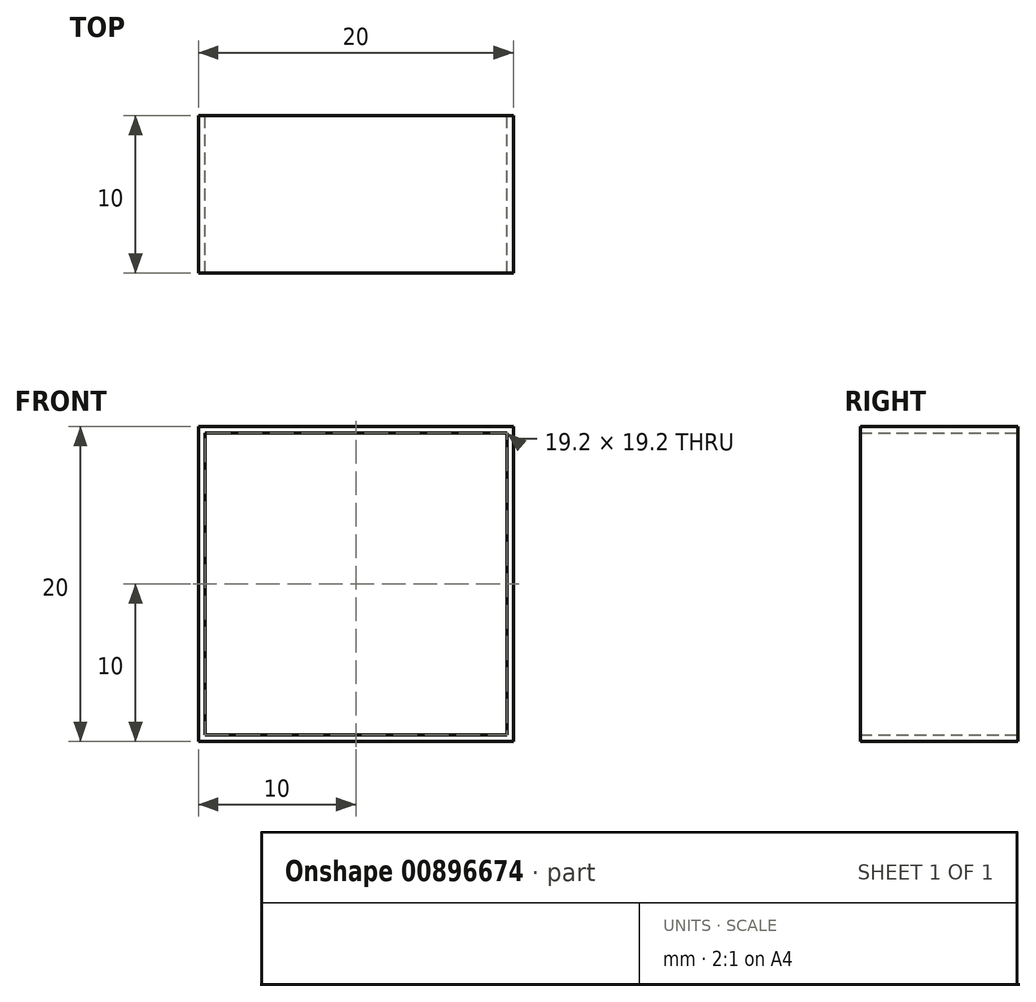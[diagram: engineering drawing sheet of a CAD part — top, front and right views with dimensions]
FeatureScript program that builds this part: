
annotation { "Feature Type Name" : "Feature", "Feature Type Description" : "" }
export const myFeature = defineFeature(function(context is Context, id is Id, definition is map)
    precondition{}
    {
        {
            var Q0;
            Q0=qCreatedBy(makeId("Front.planeOp"),FACE);
            var sketch = newSketch(context, id + "F0", { "sketchPlane" : qUnion([Q0])});
            skLineSegment(sketch, "E0.bottom", {"start": v(-10, 10) * mm, "end": v(10, 10) * mm});
            skLineSegment(sketch, "E0.top", {"start": v(-10, -10) * mm, "end": v(10, -10) * mm});
            skLineSegment(sketch, "E0.left", {"start": v(-10, 10) * mm, "end": v(-10, -10) * mm});
            skLineSegment(sketch, "E0.right", {"start": v(10, 10) * mm, "end": v(10, -10) * mm});
            skPoint(sketch, "E0.middle", {"position": v(0, 0) * mm});
            skLineSegment(sketch, "E1.0", {"start": v(-9.6, 9.6) * mm, "end": v(9.6, 9.6) * mm});
            skLineSegment(sketch, "E1.1", {"start": v(-9.6, 9.6) * mm, "end": v(-9.6, -9.6) * mm});
            skLineSegment(sketch, "E1.2", {"start": v(-9.6, -9.6) * mm, "end": v(9.6, -9.6) * mm});
            skLineSegment(sketch, "E1.3", {"start": v(9.6, 9.6) * mm, "end": v(9.6, -9.6) * mm});
            skSolve(sketch);
        }
        {
            var Q0;
            Q0=makeQuery(id+"F0.imprint","IMPRINT",FACE,{"disambiguationData":[TD([[makeQuery(id+"F0.imprint","IMPRINT",EDGE,{"derivedFrom":sQuery(id+"F0.wireOp",EDGE,"E0.bottom")}),-1.0]])]});
            extrude(context, id + "F1", {"entities" : qUnion([Q0]), "depth" : 10 * mm, "offsetDistance" : 25 * mm});
        }
    });
